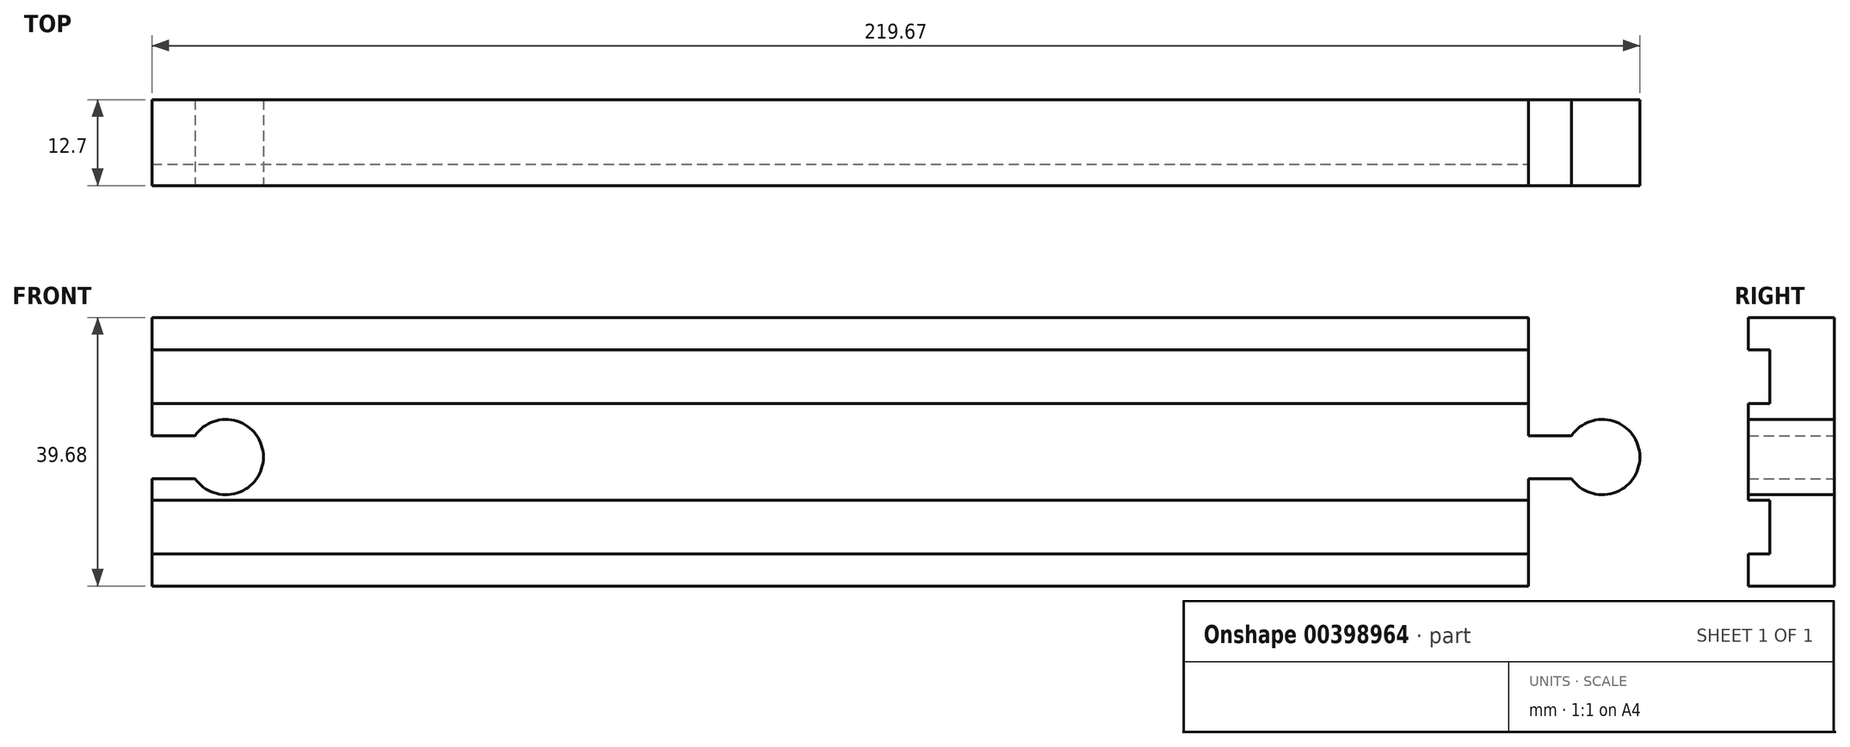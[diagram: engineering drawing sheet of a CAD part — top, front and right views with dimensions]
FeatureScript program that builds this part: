
annotation { "Feature Type Name" : "Feature", "Feature Type Description" : "" }
export const myFeature = defineFeature(function(context is Context, id is Id, definition is map)
    precondition{}
    {
        {
            var Q0;
            Q0=qCreatedBy(makeId("Front.planeOp"),FACE);
            var sketch = newSketch(context, id + "F0", { "sketchPlane" : qUnion([Q0])});
            skLineSegment(sketch, "E0.bottom", {"start": v(101.6, 19.84) * mm, "end": v(-101.6, 19.84) * mm});
            skLineSegment(sketch, "E0.top", {"start": v(101.6, -19.84) * mm, "end": v(-101.6, -19.84) * mm});
            skLineSegment(sketch, "E0.left", {"start": v(101.6, 19.84) * mm, "end": v(101.6, -19.84) * mm});
            skLineSegment(sketch, "E0.right", {"start": v(-101.6, 19.84) * mm, "end": v(-101.6, -19.84) * mm});
            skPoint(sketch, "E0.middle", {"position": v(0, 0) * mm});
            skSolve(sketch);
        }
        {
            var Q0;
            Q0 = qSketchRegion(id + "F0", true);
            extrude(context, id + "F1", {"entities" : qUnion([Q0]), "depth" : 12.7 * mm, "symmetric" : true});
        }
        {
            var Q0;
            Q0=qCreatedBy(makeId("Front.planeOp"),FACE);
            var sketch = newSketch(context, id + "F2", { "sketchPlane" : qUnion([Q0])});
            skLineSegment(sketch, "E1.0", {"start": v(101.6, 19.84) * mm, "end": v(101.6, -19.84) * mm});
            skLineSegment(sketch, "E2", {"start": v(101.6, 2.38) * mm, "end": v(107.95, 2.38) * mm});
            skLineSegment(sketch, "E3", {"start": v(101.6, -3.97) * mm, "end": v(107.95, -3.97) * mm});
            skArc(sketch, "E4", {"start": v(107.95, -3.97) * mm, "mid": v(118.07, -0.8) * mm, "end": v(107.95, 2.38) * mm});
            skSolve(sketch);
        }
        {
            var Q0;
            Q0 = qSketchRegion(id + "F2", true);
            extrude(context, id + "F3", {"entities" : qUnion([Q0]), "operationType" : NewBodyOperationType.ADD, "depth" : 12.7 * mm, "symmetric" : true});
        }
        {
            var Q0;
            Q0=qCreatedBy(makeId("Front.planeOp"),FACE);
            var sketch = newSketch(context, id + "F4", { "sketchPlane" : qUnion([Q0])});
            skLineSegment(sketch, "E5.0", {"start": v(-101.6, 19.84) * mm, "end": v(-101.6, -19.84) * mm});
            skLineSegment(sketch, "E6", {"start": v(-101.6, 2.38) * mm, "end": v(-95.25, 2.38) * mm});
            skLineSegment(sketch, "E7", {"start": v(-101.6, -3.97) * mm, "end": v(-95.25, -3.97) * mm});
            skArc(sketch, "E8", {"start": v(-95.25, -3.97) * mm, "mid": v(-85.13, -0.8) * mm, "end": v(-95.25, 2.38) * mm});
            skSolve(sketch);
        }
        {
            var Q0;
            Q0 = qSketchRegion(id + "F4", true);
            extrude(context, id + "F5", {"entities" : qUnion([Q0]), "operationType" : NewBodyOperationType.REMOVE, "oppositeDirection" : true, "depth" : 25.4 * mm, "symmetric" : true});
        }
        {
            var Q0;
            Q0=makeQuery(id+"F3.boolean.opBoolean","MERGE",FACE,{"derivedFrom":[makeQuery(id+"F1.opExtrude","CAP_FACE",FACE,{"disambiguationData":[OSD([sQuery(id+"F0.wireOp",EDGE,"E0.bottom"),sQuery(id+"F0.wireOp",EDGE,"E0.top"),sQuery(id+"F0.wireOp",EDGE,"E0.left"),sQuery(id+"F0.wireOp",EDGE,"E0.right")])],"isStart":false}),makeQuery(id+"F3.opExtrude","CAP_FACE",FACE,{"disambiguationData":[OSD([sQuery(id+"F2.wireOp",EDGE,"E1.0"),sQuery(id+"F2.wireOp",EDGE,"E2"),sQuery(id+"F2.wireOp",EDGE,"E3"),sQuery(id+"F2.wireOp",EDGE,"E4")])],"isStart":false})]});
            var sketch = newSketch(context, id + "F6", { "sketchPlane" : qUnion([Q0])});
            skLineSegment(sketch, "E9.bottom", {"start": v(-101.6, 15.08) * mm, "end": v(101.6, 15.08) * mm});
            skLineSegment(sketch, "E9.top", {"start": v(-101.6, 7.14) * mm, "end": v(101.6, 7.14) * mm});
            skLineSegment(sketch, "E9.left", {"start": v(-101.6, 15.08) * mm, "end": v(-101.6, 7.14) * mm});
            skLineSegment(sketch, "E9.right", {"start": v(101.6, 15.08) * mm, "end": v(101.6, 7.14) * mm});
            skSolve(sketch);
        }
        {
            var Q0;
            Q0 = qSketchRegion(id + "F6", true);
            extrude(context, id + "F7", {"entities" : qUnion([Q0]), "operationType" : NewBodyOperationType.REMOVE, "oppositeDirection" : true, "depth" : 3.17 * mm});
        }
        {
            var Q0;
            {var subQ0=sQuery(id+"F2.wireOp",EDGE,"E2");var subQ1=sQuery(id+"F0.wireOp",EDGE,"E0.left");var subQ2=sQuery(id+"F0.wireOp",EDGE,"E0.right");var subQ3=sQuery(id+"F2.wireOp",EDGE,"E3");var subQ4=sQuery(id+"F0.wireOp",EDGE,"E0.top");var subQ5=sQuery(id+"F2.wireOp",EDGE,"E4");Q0=makeQuery(id+"F7.boolean.opBoolean","SPLIT",FACE,{"disambiguationData":[TD([makeQuery(id+"F1.opExtrude","SWEPT_FACE",FACE,{"disambiguationData":[OSD([subQ4])]})])],"derivedFrom":makeQuery(id+"F3.boolean.opBoolean","MERGE",FACE,{"derivedFrom":[makeQuery(id+"F1.opExtrude","CAP_FACE",FACE,{"disambiguationData":[OSD([sQuery(id+"F0.wireOp",EDGE,"E0.bottom"),subQ4,subQ1,subQ2])],"isStart":false}),makeQuery(id+"F3.opExtrude","CAP_FACE",FACE,{"disambiguationData":[OSD([sQuery(id+"F2.wireOp",EDGE,"E1.0"),subQ0,subQ3,subQ5])],"isStart":false})]})});}
            var sketch = newSketch(context, id + "F8", { "sketchPlane" : qUnion([Q0])});
            skLineSegment(sketch, "E10.bottom", {"start": v(-101.6, -15.08) * mm, "end": v(101.6, -15.08) * mm});
            skLineSegment(sketch, "E10.top", {"start": v(-101.6, -7.14) * mm, "end": v(101.6, -7.14) * mm});
            skLineSegment(sketch, "E10.left", {"start": v(-101.6, -15.08) * mm, "end": v(-101.6, -7.14) * mm});
            skLineSegment(sketch, "E10.right", {"start": v(101.6, -15.08) * mm, "end": v(101.6, -7.14) * mm});
            skSolve(sketch);
        }
        {
            var Q0;
            Q0 = qSketchRegion(id + "F8", true);
            extrude(context, id + "F9", {"entities" : qUnion([Q0]), "operationType" : NewBodyOperationType.REMOVE, "oppositeDirection" : true, "depth" : 3.17 * mm});
        }
    });
